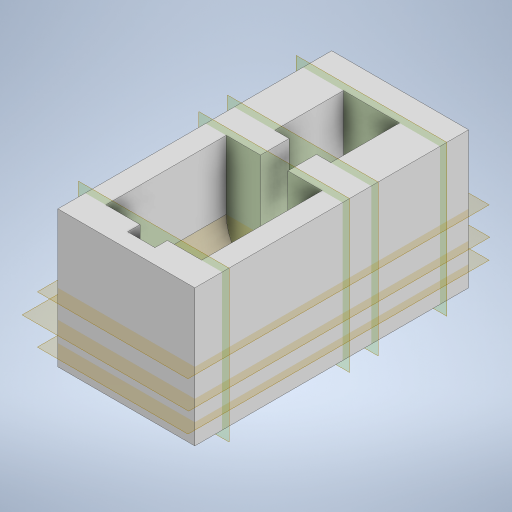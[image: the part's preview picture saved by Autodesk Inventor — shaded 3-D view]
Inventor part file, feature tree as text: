
AUTODESK INVENTOR PART (.ipt)
format: ipt  version: 2023 (Build 270158000, 158)  size: 315,904 bytes
history: native  units: in
note: dims shown in document units (in); Inventor stores cm internally (conversion verified against a paired STEP export)
features: extrude x9, plane x7, sketch x6, projected_geometry x4
ambient origin geometry x8: Origin, YZ Plane, XZ Plane, XY Plane, X Axis, Y Axis, Z Axis, Center Point
bodies: Solid1 (feature_tree)
feature tree (26):
  sketch  "Sketch1"  dims[d0=1.9685in d1=3.937in]
  extrude  "Extrusion1"  Depth=3.937in
  plane  "Work Plane3"
  plane  "Work Plane4"
  sketch  "Sketch3"  dims[d4=1.7323in d5=90.0deg]
  plane  "Work Plane5"
  plane  "Work Plane6"
  plane  "Work Plane7"
  extrude  "Extrusion5"  TaperAngle=90.0deg  [1 undecoded]
  extrude  "Extrusion6"  Depth=0.3937in
  sketch  "Sketch4"  dims[d6=1.378in d7=0.3937in]
  plane  "Work Plane8"
  extrude  "Extrusion7"  TaperAngle=90.0deg  [1 undecoded]
  extrude  "Extrusion8"  Depth=1.9685in TaperAngle=0.0deg
  extrude  "Extrusion9"  TaperAngle=90.0deg  [1 undecoded]
  extrude  "Extrusion10"  Depth=0.3937in TaperAngle=0.0deg
  plane  "Work Plane9"
  extrude  "Extrusion11"  Depth=0.3937in TaperAngle=0.0deg
  extrude  "Extrusion12"  Depth=1.378in
  projected_geometry  "Projected Loop2"
  projected_geometry  "Projected Loop3"
  sketch  "Sketch5"  dims[d8=0.9882in d9=90.0deg]
  projected_geometry  "Projected Loop4"
  sketch  "Sketch6"  dims[d10=0.8071in d11=1.9685in d12=0.0in]
  projected_geometry  "Projected Loop5"
  sketch  "Sketch7"  dims[d18=0.7953in d21=90.0deg d22=0.3937in d23=0.0in d24=0.3937in d25=0.0in d26=1.378in d27=90.0deg d28=0.3937in d29=0.0in d30=0.3937in d31=0.0in d32=0.3937in d33=2.3228in d34=0.0in d35=0.1969in d36=90.0deg d37=0.0in d38=0.0in d39=0.0in d40=0.0in d41=0.0in d42=0.7874in d43=0.3937in d44=0.1969in d45=0.7874in d46=0.3937in d47=0.0in]
note: 3 required parameter values undecoded (feature->parameter linkage not recoverable at this tier; creation-order binding heuristic only, values carry confidence <= 0.55)
